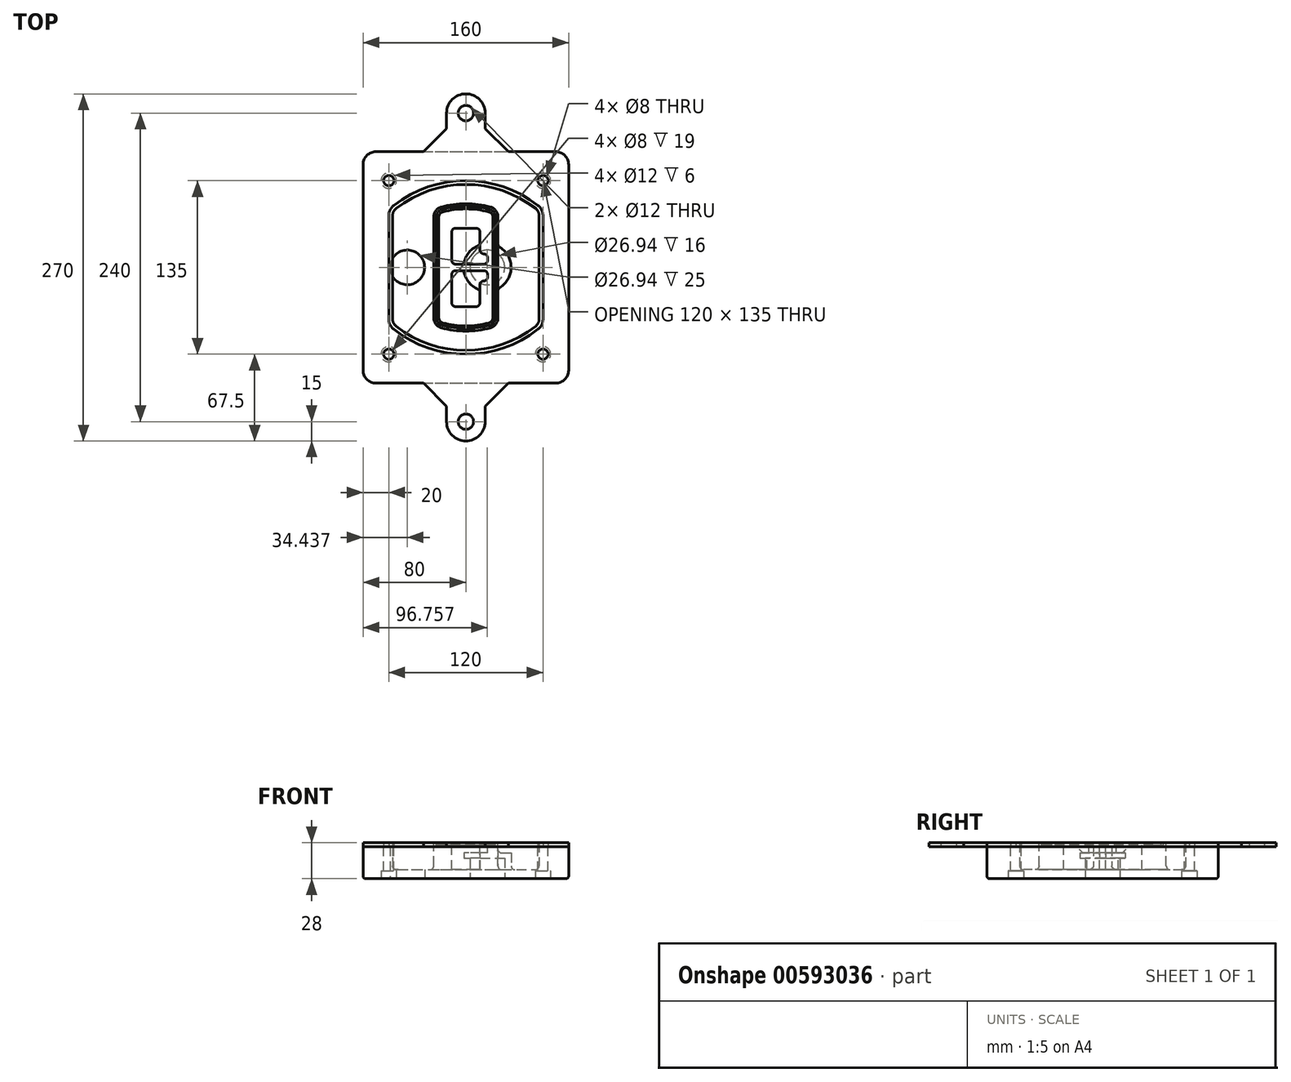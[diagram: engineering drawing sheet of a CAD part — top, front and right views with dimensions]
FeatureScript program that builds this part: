
annotation { "Feature Type Name" : "Feature", "Feature Type Description" : "" }
export const myFeature = defineFeature(function(context is Context, id is Id, definition is map)
    precondition{}
    {
        {
            var Q0;
            Q0=qCreatedBy(makeId("Top.planeOp"),FACE);
            var sketch = newSketch(context, id + "F0", { "sketchPlane" : qUnion([Q0])});
            skPoint(sketch, "E0.rect.middle", {"position": v(0, 0) * mm});
            skLineSegment(sketch, "E1.bottom", {"start": v(-70, -90) * mm, "end": v(70, -90) * mm});
            skLineSegment(sketch, "E1.top", {"start": v(-70, 90) * mm, "end": v(70, 90) * mm});
            skLineSegment(sketch, "E1.left", {"start": v(-80, -80) * mm, "end": v(-80, 80) * mm});
            skLineSegment(sketch, "E1.right", {"start": v(80, -80) * mm, "end": v(80, 80) * mm});
            skLineSegment(sketch, "E2", {"start": v(-80, 90) * mm, "end": v(80, -90) * mm, "construction": true});
            skLineSegment(sketch, "E3", {"start": v(80, 90) * mm, "end": v(-80, -90) * mm, "construction": true});
            skCircle(sketch, "E4", {"center": v(-60, 67.5) * mm, "radius": 4 * mm});
            skCircle(sketch, "E5", {"center": v(60, 67.5) * mm, "radius": 4 * mm});
            skCircle(sketch, "E6", {"center": v(60, -67.5) * mm, "radius": 4 * mm});
            skCircle(sketch, "E7", {"center": v(-60, -67.5) * mm, "radius": 4 * mm});
            skLineSegment(sketch, "E8", {"start": v(-60, 67.5) * mm, "end": v(60, 67.5) * mm, "construction": true});
            skLineSegment(sketch, "E9", {"start": v(60, 67.5) * mm, "end": v(60, -67.5) * mm, "construction": true});
            skLineSegment(sketch, "E10", {"start": v(60, -67.5) * mm, "end": v(-60, -67.5) * mm, "construction": true});
            skLineSegment(sketch, "E11", {"start": v(-60, -67.5) * mm, "end": v(-60, 67.5) * mm, "construction": true});
            skLineSegment(sketch, "E12", {"start": v(-60, 40.3) * mm, "end": v(-60, -40.3) * mm});
            skLineSegment(sketch, "E13", {"start": v(60, 40.3) * mm, "end": v(60, -40.3) * mm});
            skArc(sketch, "E14", {"start": v(56.15, 48.18) * mm, "mid": v(0, 67.5) * mm, "end": v(-56.15, 48.18) * mm});
            skArc(sketch, "E15", {"start": v(-56.15, -48.18) * mm, "mid": v(0, -67.5) * mm, "end": v(56.15, -48.18) * mm});
            skLineSegment(sketch, "E16", {"start": v(-60, 0) * mm, "end": v(60, 0) * mm, "construction": true});
            skPoint(sketch, "E17.visualSharp", {"position": v(-60, -45) * mm});
            skArc(sketch, "E17.filletArc", {"start": v(-60, -40.3) * mm, "mid": v(-58.99, -44.68) * mm, "end": v(-56.15, -48.18) * mm});
            skPoint(sketch, "E18.visualSharp", {"position": v(-60, 45) * mm});
            skArc(sketch, "E18.filletArc", {"start": v(-56.15, 48.18) * mm, "mid": v(-58.99, 44.68) * mm, "end": v(-60, 40.3) * mm});
            skPoint(sketch, "E19.visualSharp", {"position": v(60, 45) * mm});
            skArc(sketch, "E19.filletArc", {"start": v(60, 40.3) * mm, "mid": v(58.99, 44.68) * mm, "end": v(56.15, 48.18) * mm});
            skPoint(sketch, "E20.visualSharp", {"position": v(60, -45) * mm});
            skArc(sketch, "E20.filletArc", {"start": v(56.15, -48.18) * mm, "mid": v(58.99, -44.68) * mm, "end": v(60, -40.3) * mm});
            skPoint(sketch, "E21.visualSharp", {"position": v(-80, 90) * mm});
            skArc(sketch, "E21.filletArc", {"start": v(-70, 90) * mm, "mid": v(-77.07, 87.07) * mm, "end": v(-80, 80) * mm});
            skPoint(sketch, "E22.visualSharp", {"position": v(80, 90) * mm});
            skArc(sketch, "E22.filletArc", {"start": v(80, 80) * mm, "mid": v(77.07, 87.07) * mm, "end": v(70, 90) * mm});
            skPoint(sketch, "E23.visualSharp", {"position": v(80, -90) * mm});
            skArc(sketch, "E23.filletArc", {"start": v(70, -90) * mm, "mid": v(77.07, -87.07) * mm, "end": v(80, -80) * mm});
            skPoint(sketch, "E24.visualSharp", {"position": v(-80, -90) * mm});
            skArc(sketch, "E24.filletArc", {"start": v(-80, -80) * mm, "mid": v(-77.07, -87.07) * mm, "end": v(-70, -90) * mm});
            skArc(sketch, "E25.0", {"start": v(57, 40.3) * mm, "mid": v(56.3, 43.36) * mm, "end": v(54.3, 45.81) * mm});
            skLineSegment(sketch, "E25.1", {"start": v(57, 40.3) * mm, "end": v(57, -40.3) * mm});
            skArc(sketch, "E25.2", {"start": v(54.3, -45.81) * mm, "mid": v(56.3, -43.36) * mm, "end": v(57, -40.3) * mm});
            skArc(sketch, "E25.3", {"start": v(-54.3, -45.81) * mm, "mid": v(0, -64.5) * mm, "end": v(54.3, -45.81) * mm});
            skArc(sketch, "E25.4", {"start": v(-57, -40.3) * mm, "mid": v(-56.3, -43.36) * mm, "end": v(-54.3, -45.81) * mm});
            skArc(sketch, "E25.5", {"start": v(54.3, 45.81) * mm, "mid": v(0, 64.5) * mm, "end": v(-54.3, 45.81) * mm});
            skLineSegment(sketch, "E25.6", {"start": v(-57, 40.3) * mm, "end": v(-57, -40.3) * mm});
            skArc(sketch, "E25.7", {"start": v(-54.3, 45.81) * mm, "mid": v(-56.3, 43.36) * mm, "end": v(-57, 40.3) * mm});
            skArc(sketch, "E26.0", {"start": v(-58.62, 51.33) * mm, "mid": v(-62.58, 46.43) * mm, "end": v(-64, 40.3) * mm});
            skArc(sketch, "E26.1", {"start": v(58.62, 51.33) * mm, "mid": v(0, 71.5) * mm, "end": v(-58.62, 51.33) * mm});
            skArc(sketch, "E26.2", {"start": v(64, 40.3) * mm, "mid": v(62.58, 46.43) * mm, "end": v(58.62, 51.33) * mm});
            skLineSegment(sketch, "E26.3", {"start": v(64, 40.3) * mm, "end": v(64, -40.3) * mm});
            skArc(sketch, "E26.4", {"start": v(58.62, -51.33) * mm, "mid": v(62.58, -46.43) * mm, "end": v(64, -40.3) * mm});
            skLineSegment(sketch, "E26.5", {"start": v(-64, 40.3) * mm, "end": v(-64, -40.3) * mm});
            skArc(sketch, "E26.6", {"start": v(-58.62, -51.33) * mm, "mid": v(0, -71.5) * mm, "end": v(58.62, -51.33) * mm});
            skArc(sketch, "E26.7", {"start": v(-64, -40.3) * mm, "mid": v(-62.58, -46.43) * mm, "end": v(-58.62, -51.33) * mm});
            skSolve(sketch);
        }
        {
            var Q0;
            Q0=makeQuery(id+"F0.imprint","IMPRINT",FACE,{"disambiguationData":[TD([[makeQuery(id+"F0.imprint","IMPRINT",EDGE,{"derivedFrom":sQuery(id+"F0.wireOp",EDGE,"E1.bottom")}),1.0]])]});
            var Q1;
            Q1=makeQuery(id+"F0.imprint","IMPRINT",FACE,{"disambiguationData":[TD([[makeQuery(id+"F0.imprint","IMPRINT",EDGE,{"derivedFrom":sQuery(id+"F0.wireOp",EDGE,"E12")}),1.0]])]});
            var Q2;
            Q2=makeQuery(id+"F0.imprint","IMPRINT",FACE,{"disambiguationData":[TD([[makeQuery(id+"F0.imprint","IMPRINT",EDGE,{"derivedFrom":sQuery(id+"F0.wireOp",EDGE,"E25.0")}),1.0]])]});
            var Q3;
            Q3=makeQuery(id+"F0.imprint","IMPRINT",FACE,{"disambiguationData":[TD([[makeQuery(id+"F0.imprint","IMPRINT",EDGE,{"derivedFrom":sQuery(id+"F0.wireOp",EDGE,"E12")}),-1.0]])]});
            extrude(context, id + "F1", {"entities" : qUnion([Q0, Q1, Q2, Q3]), "oppositeDirection" : true, "depth" : 25 * mm});
        }
        {
            var Q0;
            Q0=makeQuery(id+"F0.imprint","IMPRINT",FACE,{"disambiguationData":[TD([[makeQuery(id+"F0.imprint","IMPRINT",EDGE,{"derivedFrom":sQuery(id+"F0.wireOp",EDGE,"E12")}),1.0]])]});
            extrude(context, id + "F2", {"entities" : qUnion([Q0]), "operationType" : NewBodyOperationType.ADD, "depth" : 3 * mm});
        }
        {
            var Q0;
            Q0=makeQuery(id+"F0.imprint","IMPRINT",FACE,{"disambiguationData":[TD([[makeQuery(id+"F0.imprint","IMPRINT",EDGE,{"derivedFrom":sQuery(id+"F0.wireOp",EDGE,"E25.0")}),1.0]])]});
            extrude(context, id + "F3", {"entities" : qUnion([Q0]), "operationType" : NewBodyOperationType.REMOVE, "oppositeDirection" : true, "depth" : 18 * mm});
        }
        {
            var Q0;
            Q0=makeQuery(id+"F2.opExtrude","CAP_FACE",FACE,{"disambiguationData":[OSD([sQuery(id+"F0.wireOp",EDGE,"E12"),sQuery(id+"F0.wireOp",EDGE,"E13"),sQuery(id+"F0.wireOp",EDGE,"E14"),sQuery(id+"F0.wireOp",EDGE,"E15"),sQuery(id+"F0.wireOp",EDGE,"E17.filletArc"),sQuery(id+"F0.wireOp",EDGE,"E18.filletArc"),sQuery(id+"F0.wireOp",EDGE,"E19.filletArc"),sQuery(id+"F0.wireOp",EDGE,"E20.filletArc"),sQuery(id+"F0.wireOp",EDGE,"E25.0"),sQuery(id+"F0.wireOp",EDGE,"E25.1"),sQuery(id+"F0.wireOp",EDGE,"E25.2"),sQuery(id+"F0.wireOp",EDGE,"E25.3"),sQuery(id+"F0.wireOp",EDGE,"E25.4"),sQuery(id+"F0.wireOp",EDGE,"E25.5"),sQuery(id+"F0.wireOp",EDGE,"E25.6"),sQuery(id+"F0.wireOp",EDGE,"E25.7")])],"isStart":false});
            var sketch = newSketch(context, id + "F4", { "sketchPlane" : qUnion([Q0])});
            skArc(sketch, "E27.0", {"start": v(-19.08, -46.97) * mm, "mid": v(0, -49.5) * mm, "end": v(19.08, -46.97) * mm});
            skArc(sketch, "E28.0", {"start": v(19.08, 46.97) * mm, "mid": v(0, 49.5) * mm, "end": v(-19.08, 46.97) * mm});
            skLineSegment(sketch, "E29", {"start": v(-25, 39.25) * mm, "end": v(-25, -39.25) * mm});
            skLineSegment(sketch, "E30", {"start": v(25, 39.25) * mm, "end": v(25, -39.25) * mm});
            skLineSegment(sketch, "E31", {"start": v(-25, 45.1) * mm, "end": v(25, 45.1) * mm, "construction": true});
            skLineSegment(sketch, "E32", {"start": v(-25, -45.1) * mm, "end": v(25, -45.1) * mm, "construction": true});
            skPoint(sketch, "E33.visualSharp", {"position": v(-25, 45.1) * mm});
            skArc(sketch, "E33.filletArc", {"start": v(-19.08, 46.97) * mm, "mid": v(-23.35, 44.11) * mm, "end": v(-25, 39.25) * mm});
            skPoint(sketch, "E34.visualSharp", {"position": v(25, 45.1) * mm});
            skArc(sketch, "E34.filletArc", {"start": v(25, 39.25) * mm, "mid": v(23.35, 44.11) * mm, "end": v(19.08, 46.97) * mm});
            skPoint(sketch, "E35.visualSharp", {"position": v(25, -45.1) * mm});
            skArc(sketch, "E35.filletArc", {"start": v(19.08, -46.97) * mm, "mid": v(23.35, -44.11) * mm, "end": v(25, -39.25) * mm});
            skPoint(sketch, "E36.visualSharp", {"position": v(-25, -45.1) * mm});
            skArc(sketch, "E36.filletArc", {"start": v(-25, -39.25) * mm, "mid": v(-23.35, -44.11) * mm, "end": v(-19.08, -46.97) * mm});
            skArc(sketch, "E37.0", {"start": v(54.3, 45.81) * mm, "mid": v(0, 64.5) * mm, "end": v(-54.3, 45.81) * mm});
            skArc(sketch, "E37.1", {"start": v(-54.3, 45.81) * mm, "mid": v(-56.3, 43.36) * mm, "end": v(-57, 40.3) * mm});
            skLineSegment(sketch, "E37.2", {"start": v(-57, 40.3) * mm, "end": v(-57, -40.3) * mm});
            skArc(sketch, "E37.3", {"start": v(-57, -40.3) * mm, "mid": v(-56.3, -43.36) * mm, "end": v(-54.3, -45.81) * mm});
            skArc(sketch, "E37.4", {"start": v(-54.3, -45.81) * mm, "mid": v(0, -64.5) * mm, "end": v(54.3, -45.81) * mm});
            skArc(sketch, "E37.5", {"start": v(54.3, -45.81) * mm, "mid": v(56.3, -43.36) * mm, "end": v(57, -40.3) * mm});
            skLineSegment(sketch, "E37.6", {"start": v(57, 40.3) * mm, "end": v(57, -40.3) * mm});
            skArc(sketch, "E37.7", {"start": v(57, 40.3) * mm, "mid": v(56.3, 43.36) * mm, "end": v(54.3, 45.81) * mm});
            skLineSegment(sketch, "E38.0", {"start": v(23, 39.25) * mm, "end": v(23, -39.25) * mm});
            skArc(sketch, "E38.1", {"start": v(18.56, -45.04) * mm, "mid": v(21.76, -42.9) * mm, "end": v(23, -39.25) * mm});
            skArc(sketch, "E38.2", {"start": v(-18.56, -45.04) * mm, "mid": v(0, -47.5) * mm, "end": v(18.56, -45.04) * mm});
            skArc(sketch, "E38.3", {"start": v(-23, -39.25) * mm, "mid": v(-21.76, -42.9) * mm, "end": v(-18.56, -45.04) * mm});
            skLineSegment(sketch, "E38.4", {"start": v(-23, 39.25) * mm, "end": v(-23, -39.25) * mm});
            skArc(sketch, "E38.5", {"start": v(23, 39.25) * mm, "mid": v(21.76, 42.9) * mm, "end": v(18.56, 45.04) * mm});
            skArc(sketch, "E38.6", {"start": v(-18.56, 45.04) * mm, "mid": v(-21.76, 42.9) * mm, "end": v(-23, 39.25) * mm});
            skArc(sketch, "E38.7", {"start": v(18.56, 45.04) * mm, "mid": v(0, 47.5) * mm, "end": v(-18.56, 45.04) * mm});
            skArc(sketch, "E39.0", {"start": v(21, 39.25) * mm, "mid": v(20.18, 41.68) * mm, "end": v(18.04, 43.1) * mm});
            skLineSegment(sketch, "E39.1", {"start": v(21, 39.25) * mm, "end": v(21, -39.25) * mm});
            skArc(sketch, "E39.2", {"start": v(18.04, -43.1) * mm, "mid": v(20.18, -41.68) * mm, "end": v(21, -39.25) * mm});
            skArc(sketch, "E39.3", {"start": v(-18.04, -43.1) * mm, "mid": v(0, -45.5) * mm, "end": v(18.04, -43.1) * mm});
            skArc(sketch, "E39.4", {"start": v(-21, -39.25) * mm, "mid": v(-20.18, -41.68) * mm, "end": v(-18.04, -43.1) * mm});
            skArc(sketch, "E39.5", {"start": v(18.04, 43.1) * mm, "mid": v(0, 45.5) * mm, "end": v(-18.04, 43.1) * mm});
            skLineSegment(sketch, "E39.6", {"start": v(-21, 39.25) * mm, "end": v(-21, -39.25) * mm});
            skArc(sketch, "E39.7", {"start": v(-18.04, 43.1) * mm, "mid": v(-20.18, 41.68) * mm, "end": v(-21, 39.25) * mm});
            skLineSegment(sketch, "E40", {"start": v(-25, 0) * mm, "end": v(25, 0) * mm, "construction": true});
            skLineSegment(sketch, "E41", {"start": v(-11, 5.5) * mm, "end": v(-11, 27.5) * mm});
            skLineSegment(sketch, "E42", {"start": v(-8, 30.5) * mm, "end": v(8, 30.5) * mm});
            skLineSegment(sketch, "E43", {"start": v(11, 27.5) * mm, "end": v(11, 13.5) * mm});
            skLineSegment(sketch, "E44", {"start": v(14, 10.5) * mm, "end": v(14, 10.5) * mm});
            skLineSegment(sketch, "E45", {"start": v(17, 7.5) * mm, "end": v(17, 5.5) * mm});
            skLineSegment(sketch, "E46", {"start": v(14, 2.5) * mm, "end": v(-8, 2.5) * mm});
            skPoint(sketch, "E47.visualSharp", {"position": v(-11, 30.5) * mm});
            skArc(sketch, "E47.filletArc", {"start": v(-8, 30.5) * mm, "mid": v(-10.12, 29.62) * mm, "end": v(-11, 27.5) * mm});
            skPoint(sketch, "E48.visualSharp", {"position": v(11, 30.5) * mm});
            skArc(sketch, "E48.filletArc", {"start": v(11, 27.5) * mm, "mid": v(10.12, 29.62) * mm, "end": v(8, 30.5) * mm});
            skPoint(sketch, "E49.visualSharp", {"position": v(11, 10.5) * mm});
            skArc(sketch, "E49.filletArc", {"start": v(11, 13.5) * mm, "mid": v(11.88, 11.38) * mm, "end": v(14, 10.5) * mm});
            skPoint(sketch, "E50.visualSharp", {"position": v(17, 10.5) * mm});
            skArc(sketch, "E50.filletArc", {"start": v(17, 7.5) * mm, "mid": v(16.12, 9.62) * mm, "end": v(14, 10.5) * mm});
            skPoint(sketch, "E51.visualSharp", {"position": v(17, 2.5) * mm});
            skArc(sketch, "E51.filletArc", {"start": v(14, 2.5) * mm, "mid": v(16.12, 3.38) * mm, "end": v(17, 5.5) * mm});
            skPoint(sketch, "E52.visualSharp", {"position": v(-11, 2.5) * mm});
            skArc(sketch, "E52.filletArc", {"start": v(-11, 5.5) * mm, "mid": v(-10.12, 3.38) * mm, "end": v(-8, 2.5) * mm});
            skLineSegment(sketch, "E53.0.MirrorCS", {"start": v(14, -2.5) * mm, "end": v(-8, -2.5) * mm});
            skArc(sketch, "E54.0.MirrorCS", {"start": v(-11, -5.5) * mm, "mid": v(-10.12, -3.38) * mm, "end": v(-8, -2.5) * mm});
            skLineSegment(sketch, "E55.0.MirrorCS", {"start": v(-11, -5.5) * mm, "end": v(-11, -27.5) * mm});
            skArc(sketch, "E56.0.MirrorCS", {"start": v(-8, -30.5) * mm, "mid": v(-10.12, -29.62) * mm, "end": v(-11, -27.5) * mm});
            skLineSegment(sketch, "E57.0.MirrorCS", {"start": v(-8, -30.5) * mm, "end": v(8, -30.5) * mm});
            skArc(sketch, "E58.0.MirrorCS", {"start": v(11, -27.5) * mm, "mid": v(10.12, -29.62) * mm, "end": v(8, -30.5) * mm});
            skLineSegment(sketch, "E59.0.MirrorCS", {"start": v(11, -27.5) * mm, "end": v(11, -13.5) * mm});
            skArc(sketch, "E60.0.MirrorCS", {"start": v(11, -13.5) * mm, "mid": v(11.88, -11.38) * mm, "end": v(14, -10.5) * mm});
            skArc(sketch, "E61.0.MirrorCS", {"start": v(17, -7.5) * mm, "mid": v(16.12, -9.62) * mm, "end": v(14, -10.5) * mm});
            skLineSegment(sketch, "E62.0.MirrorCS", {"start": v(17, -7.5) * mm, "end": v(17, -5.5) * mm});
            skArc(sketch, "E63.0.MirrorCS", {"start": v(14, -2.5) * mm, "mid": v(16.12, -3.38) * mm, "end": v(17, -5.5) * mm});
            skSolve(sketch);
        }
        {
            var Q0;
            Q0=makeQuery(id+"F4.imprint","IMPRINT",FACE,{"disambiguationData":[TD([[makeQuery(id+"F4.imprint","IMPRINT",EDGE,{"derivedFrom":sQuery(id+"F4.wireOp",EDGE,"E27.0")}),1.0]])]});
            var Q1;
            Q1=makeQuery(id+"F4.imprint","IMPRINT",FACE,{"disambiguationData":[TD([[makeQuery(id+"F4.imprint","IMPRINT",EDGE,{"derivedFrom":sQuery(id+"F4.wireOp",EDGE,"E38.0")}),-1.0]])]});
            var Q2;
            Q2=makeQuery(id+"F4.imprint","IMPRINT",FACE,{"disambiguationData":[TD([[makeQuery(id+"F4.imprint","IMPRINT",EDGE,{"derivedFrom":sQuery(id+"F4.wireOp",EDGE,"E39.0")}),1.0]])]});
            extrude(context, id + "F5", {"entities" : qUnion([Q0, Q1, Q2]), "operationType" : NewBodyOperationType.ADD, "endBound" : BoundingType.UP_TO_NEXT, "oppositeDirection" : true, "depth" : 25 * mm});
        }
        {
            var Q0;
            Q0=makeQuery(id+"F4.imprint","IMPRINT",FACE,{"disambiguationData":[TD([[makeQuery(id+"F4.imprint","IMPRINT",EDGE,{"derivedFrom":sQuery(id+"F4.wireOp",EDGE,"E38.0")}),-1.0]])]});
            extrude(context, id + "F6", {"entities" : qUnion([Q0]), "operationType" : NewBodyOperationType.REMOVE, "oppositeDirection" : true, "depth" : 2 * mm});
        }
        {
            var Q0;
            Q0=makeQuery(id+"F1.opExtrude","CAP_FACE",FACE,{"disambiguationData":[OSD([sQuery(id+"F0.wireOp",EDGE,"E1.bottom"),sQuery(id+"F0.wireOp",EDGE,"E1.top"),sQuery(id+"F0.wireOp",EDGE,"E1.left"),sQuery(id+"F0.wireOp",EDGE,"E1.right"),sQuery(id+"F0.wireOp",EDGE,"E4"),sQuery(id+"F0.wireOp",EDGE,"E5"),sQuery(id+"F0.wireOp",EDGE,"E6"),sQuery(id+"F0.wireOp",EDGE,"E7"),sQuery(id+"F0.wireOp",EDGE,"E21.filletArc"),sQuery(id+"F0.wireOp",EDGE,"E22.filletArc"),sQuery(id+"F0.wireOp",EDGE,"E23.filletArc"),sQuery(id+"F0.wireOp",EDGE,"E24.filletArc")])],"isStart":false});
            var sketch = newSketch(context, id + "F7", { "sketchPlane" : qUnion([Q0])});
            skCircle(sketch, "E64", {"center": v(16.76, 0) * mm, "radius": 13.47 * mm});
            skCircle(sketch, "E65", {"center": v(-45.56, 0) * mm, "radius": 13.47 * mm});
            skLineSegment(sketch, "E66", {"start": v(80, 0) * mm, "end": v(-80, 0) * mm});
            skCircle(sketch, "E67", {"center": v(16.76, 0) * mm, "radius": 18.47 * mm});
            skCircle(sketch, "E68", {"center": v(60, -67.5) * mm, "radius": 6 * mm});
            skCircle(sketch, "E69", {"center": v(-60, -67.5) * mm, "radius": 6 * mm});
            skCircle(sketch, "E70", {"center": v(-60, 67.5) * mm, "radius": 6 * mm});
            skCircle(sketch, "E71", {"center": v(60, 67.5) * mm, "radius": 6 * mm});
            skSolve(sketch);
        }
        {
            var Q0;
            {var subQ1=sQuery(id+"F7.wireOp",EDGE,"E66");var subQ4=sQuery(id+"F7.wireOp",EDGE,"E64");var subQ6=makeQuery(id+"F7.imprint","INTERSECT",VERTEX,{"disambiguationData":[OD(0.0)],"derivedFrom":[subQ4,subQ1]});Q0=makeQuery(id+"F7.imprint","IMPRINT",FACE,{"disambiguationData":[TD([[makeQuery(id+"F7.imprint","IMPRINT",EDGE,{"disambiguationData":[TD([[subQ6,-1.0]])],"derivedFrom":subQ4}),-1.0]])]});}
            var Q1;
            {var subQ0=sQuery(id+"F7.wireOp",EDGE,"E66");var subQ1=sQuery(id+"F7.wireOp",EDGE,"E64");var subQ3=makeQuery(id+"F7.imprint","INTERSECT",VERTEX,{"disambiguationData":[OD(0.0)],"derivedFrom":[subQ1,subQ0]});Q1=makeQuery(id+"F7.imprint","IMPRINT",FACE,{"disambiguationData":[TD([[makeQuery(id+"F7.imprint","IMPRINT",EDGE,{"disambiguationData":[TD([[subQ3,-1.0]])],"derivedFrom":subQ1}),1.0]])]});}
            var Q2;
            {var subQ0=sQuery(id+"F7.wireOp",EDGE,"E66");var subQ1=sQuery(id+"F7.wireOp",EDGE,"E64");var subQ3=makeQuery(id+"F7.imprint","INTERSECT",VERTEX,{"disambiguationData":[OD(0.0)],"derivedFrom":[subQ1,subQ0]});Q2=makeQuery(id+"F7.imprint","IMPRINT",FACE,{"disambiguationData":[TD([[makeQuery(id+"F7.imprint","IMPRINT",EDGE,{"disambiguationData":[TD([[subQ3,1.0]])],"derivedFrom":subQ1}),1.0]])]});}
            var Q3;
            {var subQ1=sQuery(id+"F7.wireOp",EDGE,"E66");var subQ4=sQuery(id+"F7.wireOp",EDGE,"E64");var subQ6=makeQuery(id+"F7.imprint","INTERSECT",VERTEX,{"disambiguationData":[OD(0.0)],"derivedFrom":[subQ4,subQ1]});Q3=makeQuery(id+"F7.imprint","IMPRINT",FACE,{"disambiguationData":[TD([[makeQuery(id+"F7.imprint","IMPRINT",EDGE,{"disambiguationData":[TD([[subQ6,1.0]])],"derivedFrom":subQ4}),-1.0]])]});}
            extrude(context, id + "F8", {"entities" : qUnion([Q0, Q1, Q2, Q3]), "operationType" : NewBodyOperationType.ADD, "oppositeDirection" : true, "depth" : 20 * mm});
        }
        {
            var Q0;
            {var subQ0=sQuery(id+"F7.wireOp",EDGE,"E66");var subQ1=sQuery(id+"F7.wireOp",EDGE,"E64");var subQ3=makeQuery(id+"F7.imprint","INTERSECT",VERTEX,{"disambiguationData":[OD(0.0)],"derivedFrom":[subQ1,subQ0]});Q0=makeQuery(id+"F7.imprint","IMPRINT",FACE,{"disambiguationData":[TD([[makeQuery(id+"F7.imprint","IMPRINT",EDGE,{"disambiguationData":[TD([[subQ3,-1.0]])],"derivedFrom":subQ1}),1.0]])]});}
            var Q1;
            {var subQ0=sQuery(id+"F7.wireOp",EDGE,"E66");var subQ1=sQuery(id+"F7.wireOp",EDGE,"E64");var subQ3=makeQuery(id+"F7.imprint","INTERSECT",VERTEX,{"disambiguationData":[OD(0.0)],"derivedFrom":[subQ1,subQ0]});Q1=makeQuery(id+"F7.imprint","IMPRINT",FACE,{"disambiguationData":[TD([[makeQuery(id+"F7.imprint","IMPRINT",EDGE,{"disambiguationData":[TD([[subQ3,1.0]])],"derivedFrom":subQ1}),1.0]])]});}
            extrude(context, id + "F9", {"entities" : qUnion([Q0, Q1]), "operationType" : NewBodyOperationType.REMOVE, "oppositeDirection" : true, "depth" : 16 * mm});
        }
        {
            var Q0;
            {var subQ0=sQuery(id+"F7.wireOp",EDGE,"E66");var subQ1=sQuery(id+"F7.wireOp",EDGE,"E65");var subQ3=makeQuery(id+"F7.imprint","INTERSECT",VERTEX,{"disambiguationData":[OD(0.0)],"derivedFrom":[subQ1,subQ0]});Q0=makeQuery(id+"F7.imprint","IMPRINT",FACE,{"disambiguationData":[TD([[makeQuery(id+"F7.imprint","IMPRINT",EDGE,{"disambiguationData":[TD([[subQ3,-1.0]])],"derivedFrom":subQ1}),1.0]])]});}
            var Q1;
            {var subQ0=sQuery(id+"F7.wireOp",EDGE,"E66");var subQ1=sQuery(id+"F7.wireOp",EDGE,"E65");var subQ3=makeQuery(id+"F7.imprint","INTERSECT",VERTEX,{"disambiguationData":[OD(0.0)],"derivedFrom":[subQ1,subQ0]});Q1=makeQuery(id+"F7.imprint","IMPRINT",FACE,{"disambiguationData":[TD([[makeQuery(id+"F7.imprint","IMPRINT",EDGE,{"disambiguationData":[TD([[subQ3,1.0]])],"derivedFrom":subQ1}),1.0]])]});}
            extrude(context, id + "F10", {"entities" : qUnion([Q0, Q1]), "operationType" : NewBodyOperationType.REMOVE, "oppositeDirection" : true, "depth" : 25 * mm});
        }
        {
            var Q0;
            Q0=makeQuery(id+"F7.imprint","IMPRINT",FACE,{"disambiguationData":[TD([[makeQuery(id+"F7.imprint","IMPRINT",EDGE,{"derivedFrom":sQuery(id+"F7.wireOp",EDGE,"E68")}),1.0]])]});
            var Q1;
            Q1=makeQuery(id+"F7.imprint","IMPRINT",FACE,{"disambiguationData":[TD([[makeQuery(id+"F7.imprint","IMPRINT",EDGE,{"derivedFrom":makeQuery(id+"F1.opExtrude","CAP_EDGE",EDGE,{"disambiguationData":[OSD([sQuery(id+"F0.wireOp",EDGE,"E5")])],"isStart":false})}),-1.0]])]});
            var Q2;
            Q2=makeQuery(id+"F7.imprint","IMPRINT",FACE,{"disambiguationData":[TD([[makeQuery(id+"F7.imprint","IMPRINT",EDGE,{"derivedFrom":sQuery(id+"F7.wireOp",EDGE,"E69")}),1.0]])]});
            var Q3;
            Q3=makeQuery(id+"F7.imprint","IMPRINT",FACE,{"disambiguationData":[TD([[makeQuery(id+"F7.imprint","IMPRINT",EDGE,{"derivedFrom":makeQuery(id+"F1.opExtrude","CAP_EDGE",EDGE,{"disambiguationData":[OSD([sQuery(id+"F0.wireOp",EDGE,"E4")])],"isStart":false})}),-1.0]])]});
            var Q4;
            Q4=makeQuery(id+"F7.imprint","IMPRINT",FACE,{"disambiguationData":[TD([[makeQuery(id+"F7.imprint","IMPRINT",EDGE,{"derivedFrom":sQuery(id+"F7.wireOp",EDGE,"E70")}),1.0]])]});
            var Q5;
            Q5=makeQuery(id+"F7.imprint","IMPRINT",FACE,{"disambiguationData":[TD([[makeQuery(id+"F7.imprint","IMPRINT",EDGE,{"derivedFrom":makeQuery(id+"F1.opExtrude","CAP_EDGE",EDGE,{"disambiguationData":[OSD([sQuery(id+"F0.wireOp",EDGE,"E7")])],"isStart":false})}),-1.0]])]});
            var Q6;
            Q6=makeQuery(id+"F7.imprint","IMPRINT",FACE,{"disambiguationData":[TD([[makeQuery(id+"F7.imprint","IMPRINT",EDGE,{"derivedFrom":sQuery(id+"F7.wireOp",EDGE,"E71")}),1.0]])]});
            var Q7;
            Q7=makeQuery(id+"F7.imprint","IMPRINT",FACE,{"disambiguationData":[TD([[makeQuery(id+"F7.imprint","IMPRINT",EDGE,{"derivedFrom":makeQuery(id+"F1.opExtrude","CAP_EDGE",EDGE,{"disambiguationData":[OSD([sQuery(id+"F0.wireOp",EDGE,"E6")])],"isStart":false})}),-1.0]])]});
            extrude(context, id + "F11", {"entities" : qUnion([Q0, Q1, Q2, Q3, Q4, Q5, Q6, Q7]), "operationType" : NewBodyOperationType.REMOVE, "oppositeDirection" : true, "depth" : 6 * mm});
        }
        {
            var Q0;
            Q0=makeQuery(id+"F9.boolean.opBoolean","COPY",FACE,{"derivedFrom":makeQuery(id+"F9.opExtrude","CAP_FACE",FACE,{"disambiguationData":[OSD([sQuery(id+"F7.wireOp",EDGE,"E64")])],"isStart":false})});
            var sketch = newSketch(context, id + "F12", { "sketchPlane" : qUnion([Q0])});
            skArc(sketch, "E72.0", {"start": v(11, 17.55) * mm, "mid": v(2.57, 11.82) * mm, "end": v(-1.54, 2.5) * mm});
            skArc(sketch, "E72.1", {"start": v(-1.54, -2.5) * mm, "mid": v(2.57, -11.82) * mm, "end": v(11, -17.55) * mm});
            skLineSegment(sketch, "E73", {"start": v(-1.54, -2.5) * mm, "end": v(14, -2.5) * mm});
            skLineSegment(sketch, "E74.0", {"start": v(14, 2.5) * mm, "end": v(-1.54, 2.5) * mm});
            skArc(sketch, "E74.1", {"start": v(14, 2.5) * mm, "mid": v(16.12, 3.38) * mm, "end": v(17, 5.5) * mm});
            skLineSegment(sketch, "E74.2", {"start": v(17, 7.5) * mm, "end": v(17, 5.5) * mm});
            skArc(sketch, "E74.3", {"start": v(17, 7.5) * mm, "mid": v(16.12, 9.62) * mm, "end": v(14, 10.5) * mm});
            skArc(sketch, "E74.4", {"start": v(11, 13.5) * mm, "mid": v(11.88, 11.38) * mm, "end": v(14, 10.5) * mm});
            skLineSegment(sketch, "E74.5", {"start": v(11, 17.55) * mm, "end": v(11, 13.5) * mm});
            skLineSegment(sketch, "E74.7", {"start": v(14, -2.5) * mm, "end": v(-1.54, -2.5) * mm});
            skArc(sketch, "E74.8", {"start": v(14, -2.5) * mm, "mid": v(16.12, -3.38) * mm, "end": v(17, -5.5) * mm});
            skLineSegment(sketch, "E74.9", {"start": v(17, -7.5) * mm, "end": v(17, -5.5) * mm});
            skArc(sketch, "E74.10", {"start": v(17, -7.5) * mm, "mid": v(16.12, -9.62) * mm, "end": v(14, -10.5) * mm});
            skArc(sketch, "E74.11", {"start": v(11, -13.5) * mm, "mid": v(11.88, -11.38) * mm, "end": v(14, -10.5) * mm});
            skLineSegment(sketch, "E74.12", {"start": v(11, -17.55) * mm, "end": v(11, -13.5) * mm});
            skPoint(sketch, "E75.orphan", {"position": v(11, -27.5) * mm});
            skPoint(sketch, "E76.orphan", {"position": v(-8, -2.5) * mm});
            skPoint(sketch, "E77.orphan", {"position": v(-8, 2.5) * mm});
            skPoint(sketch, "E78.orphan", {"position": v(11, 27.5) * mm});
            skSolve(sketch);
        }
        {
            var Q0;
            {var subQ7=sQuery(id+"F12.wireOp",EDGE,"E72.0");var subQ14=sQuery(id+"F12.wireOp",EDGE,"E72.1");var subQ16=sQuery(id+"F12.wireOp",EDGE,"E74.1");var subQ18=sQuery(id+"F12.wireOp",EDGE,"E74.8");Q0=qUnion([makeQuery(id+"F12.imprint","IMPRINT",FACE,{"disambiguationData":[TD([[makeQuery(id+"F12.imprint","IMPRINT",EDGE,{"derivedFrom":subQ7}),1.0]])]}),makeQuery(id+"F12.imprint","IMPRINT",FACE,{"disambiguationData":[TD([[makeQuery(id+"F12.imprint","IMPRINT",EDGE,{"derivedFrom":subQ14}),1.0]])]}),makeQuery(id+"F12.imprint","IMPRINT",FACE,{"disambiguationData":[TD([[makeQuery(id+"F12.imprint","IMPRINT",EDGE,{"derivedFrom":subQ16}),1.0]])]}),makeQuery(id+"F12.imprint","IMPRINT",FACE,{"disambiguationData":[TD([[makeQuery(id+"F12.imprint","IMPRINT",EDGE,{"derivedFrom":subQ18}),-1.0]])]})]);}
            var Q1;
            Q1=makeQuery(id+"F5.boolean.opBoolean","SPLIT",FACE,{"disambiguationData":[TD([makeQuery(id+"F5.opExtrude","SWEPT_FACE",FACE,{"disambiguationData":[OSD([sQuery(id+"F4.wireOp",EDGE,"E41")])]})])],"derivedFrom":makeQuery(id+"F3.boolean.opBoolean","COPY",FACE,{"derivedFrom":makeQuery(id+"F3.opExtrude","CAP_FACE",FACE,{"disambiguationData":[OSD([sQuery(id+"F0.wireOp",EDGE,"E25.0"),sQuery(id+"F0.wireOp",EDGE,"E25.1"),sQuery(id+"F0.wireOp",EDGE,"E25.2"),sQuery(id+"F0.wireOp",EDGE,"E25.3"),sQuery(id+"F0.wireOp",EDGE,"E25.4"),sQuery(id+"F0.wireOp",EDGE,"E25.5"),sQuery(id+"F0.wireOp",EDGE,"E25.6"),sQuery(id+"F0.wireOp",EDGE,"E25.7")])],"isStart":false})})});
            extrude(context, id + "F13", {"entities" : qUnion([Q0]), "operationType" : NewBodyOperationType.REMOVE, "endBound" : BoundingType.UP_TO_SURFACE, "endBoundEntityFace" : qUnion([Q1]), "depth" : 25 * mm});
        }
        {
            var Q0;
            Q0=makeQuery(id+"F3.boolean.opBoolean","COPY",EDGE,{"derivedFrom":makeQuery(id+"F3.opExtrude","CAP_EDGE",EDGE,{"disambiguationData":[OSD([sQuery(id+"F0.wireOp",EDGE,"E25.6")])],"isStart":false})});
            var Q1;
            Q1=makeQuery(id+"F8.boolean.opBoolean","INTERSECT",EDGE,{"derivedFrom":[makeQuery(id+"F5.opExtrude","SWEPT_FACE",FACE,{"disambiguationData":[OSD([sQuery(id+"F4.wireOp",EDGE,"E30")])]}),makeQuery(id+"F8.opExtrude","CAP_FACE",FACE,{"disambiguationData":[OSD([sQuery(id+"F7.wireOp",EDGE,"E67")])],"isStart":false})]});
            var Q2;
            Q2=makeQuery(id+"F8.boolean.opBoolean","INTERSECT",EDGE,{"disambiguationData":[OD(1.0)],"derivedFrom":[makeQuery(id+"F5.opExtrude","SWEPT_FACE",FACE,{"disambiguationData":[OSD([sQuery(id+"F4.wireOp",EDGE,"E30")])]}),makeQuery(id+"F8.opExtrude","SWEPT_FACE",FACE,{"disambiguationData":[OSD([sQuery(id+"F7.wireOp",EDGE,"E67")])]})]});
            var Q3;
            {var subQ0=sQuery(id+"F4.wireOp",EDGE,"E30");Q3=makeQuery(id+"F8.boolean.opBoolean","SPLIT",EDGE,{"disambiguationData":[TD([makeQuery(id+"F5.opExtrude","SWEPT_FACE",FACE,{"disambiguationData":[OSD([sQuery(id+"F4.wireOp",EDGE,"E35.filletArc")])]})])],"derivedFrom":makeQuery(id+"F5.opExtrude","CAP_EDGE",EDGE,{"disambiguationData":[OSD([subQ0])],"isStart":false})});}
            var Q4;
            {var subQ0=sQuery(id+"F0.wireOp",EDGE,"E25.7");var subQ1=sQuery(id+"F0.wireOp",EDGE,"E25.1");var subQ2=sQuery(id+"F0.wireOp",EDGE,"E25.6");var subQ3=sQuery(id+"F0.wireOp",EDGE,"E25.5");var subQ4=sQuery(id+"F0.wireOp",EDGE,"E25.4");var subQ5=sQuery(id+"F0.wireOp",EDGE,"E25.0");var subQ6=sQuery(id+"F0.wireOp",EDGE,"E25.2");var subQ7=sQuery(id+"F0.wireOp",EDGE,"E25.3");Q4=makeQuery(id+"F8.boolean.opBoolean","INTERSECT",EDGE,{"derivedFrom":[makeQuery(id+"F5.boolean.opBoolean","SPLIT",FACE,{"disambiguationData":[TD([makeQuery(id+"F2.opExtrude","SWEPT_FACE",FACE,{"disambiguationData":[OSD([subQ5])]})])],"derivedFrom":makeQuery(id+"F3.boolean.opBoolean","COPY",FACE,{"derivedFrom":makeQuery(id+"F3.opExtrude","CAP_FACE",FACE,{"disambiguationData":[OSD([subQ5,subQ1,subQ6,subQ7,subQ4,subQ3,subQ2,subQ0])],"isStart":false})})}),makeQuery(id+"F8.opExtrude","SWEPT_FACE",FACE,{"disambiguationData":[OSD([sQuery(id+"F7.wireOp",EDGE,"E67")])]})]});}
            var Q5;
            Q5=makeQuery(id+"F8.boolean.opBoolean","INTERSECT",EDGE,{"disambiguationData":[OD(0.0)],"derivedFrom":[makeQuery(id+"F5.opExtrude","SWEPT_FACE",FACE,{"disambiguationData":[OSD([sQuery(id+"F4.wireOp",EDGE,"E30")])]}),makeQuery(id+"F8.opExtrude","SWEPT_FACE",FACE,{"disambiguationData":[OSD([sQuery(id+"F7.wireOp",EDGE,"E67")])]})]});
            fillet(context, id + "F14", {"entities" : qUnion([Q0, Q1, Q2, Q3, Q4, Q5]), "radius" : 3 * mm, "tangentPropagation" : true, "allowEdgeOverflow" : false});
        }
        {
            var Q0;
            Q0=makeQuery(id+"F1.opExtrude","CAP_EDGE",EDGE,{"disambiguationData":[OSD([sQuery(id+"F0.wireOp",EDGE,"E1.bottom")])],"isStart":false});
            fillet(context, id + "F15", {"entities" : qUnion([Q0]), "radius" : 2 * mm, "tangentPropagation" : true, "allowEdgeOverflow" : false});
        }
        {
            var Q0;
            {var subQ0=sQuery(id+"F0.wireOp",EDGE,"E21.filletArc");var subQ1=sQuery(id+"F0.wireOp",EDGE,"E7");var subQ2=sQuery(id+"F0.wireOp",EDGE,"E6");var subQ3=sQuery(id+"F0.wireOp",EDGE,"E5");var subQ4=sQuery(id+"F0.wireOp",EDGE,"E4");var subQ5=sQuery(id+"F0.wireOp",EDGE,"E22.filletArc");var subQ6=sQuery(id+"F0.wireOp",EDGE,"E1.bottom");var subQ7=sQuery(id+"F0.wireOp",EDGE,"E1.right");var subQ8=sQuery(id+"F0.wireOp",EDGE,"E1.top");var subQ9=sQuery(id+"F0.wireOp",EDGE,"E1.left");var subQ10=sQuery(id+"F0.wireOp",EDGE,"E23.filletArc");var subQ11=sQuery(id+"F0.wireOp",EDGE,"E24.filletArc");Q0=makeQuery(id+"F2.boolean.opBoolean","SPLIT",FACE,{"disambiguationData":[TD([makeQuery(id+"F1.opExtrude","SWEPT_FACE",FACE,{"disambiguationData":[OSD([subQ6])]})])],"derivedFrom":makeQuery(id+"F1.opExtrude","CAP_FACE",FACE,{"disambiguationData":[OSD([subQ6,subQ8,subQ9,subQ7,subQ4,subQ3,subQ2,subQ1,subQ0,subQ5,subQ10,subQ11])],"isStart":true})});}
            var sketch = newSketch(context, id + "F16", { "sketchPlane" : qUnion([Q0])});
            skLineSegment(sketch, "E79", {"start": v(0, 90) * mm, "end": v(0, 120) * mm, "construction": true});
            skLineSegment(sketch, "E80", {"start": v(-15, 120) * mm, "end": v(-15, 108) * mm});
            skLineSegment(sketch, "E81", {"start": v(-15, 108) * mm, "end": v(-33, 90) * mm});
            skLineSegment(sketch, "E82.MirrorCS", {"start": v(15, 120) * mm, "end": v(15, 108) * mm});
            skLineSegment(sketch, "E83.MirrorCS", {"start": v(15, 108) * mm, "end": v(33, 90) * mm});
            skArc(sketch, "E84", {"start": v(-15, 120) * mm, "mid": v(0, 135) * mm, "end": v(15, 120) * mm});
            skLineSegment(sketch, "E85", {"start": v(0, 0) * mm, "end": v(-111.77, 0) * mm, "construction": true});
            skLineSegment(sketch, "E86.MirrorCS", {"start": v(-15, -120) * mm, "end": v(-15, -108) * mm});
            skLineSegment(sketch, "E87.MirrorCS", {"start": v(-15, -108) * mm, "end": v(-33, -90) * mm});
            skArc(sketch, "E88.MirrorCS", {"start": v(-15, -120) * mm, "mid": v(0, -135) * mm, "end": v(15, -120) * mm, "construction": true});
            skArc(sketch, "E89.MirrorCS", {"start": v(-15, -120) * mm, "mid": v(0, -135) * mm, "end": v(15, -120) * mm});
            skLineSegment(sketch, "E90.MirrorCS", {"start": v(15, -120) * mm, "end": v(15, -108) * mm});
            skLineSegment(sketch, "E91.MirrorCS", {"start": v(15, -108) * mm, "end": v(33, -90) * mm});
            skCircle(sketch, "E92", {"center": v(0, 120) * mm, "radius": 6 * mm});
            skCircle(sketch, "E93.MirrorC", {"center": v(0, -120) * mm, "radius": 6 * mm});
            skSolve(sketch);
        }
        {
            var Q0;
            Q0=makeQuery(id+"F16.imprint","IMPRINT",FACE,{"disambiguationData":[TD([[makeQuery(id+"F16.imprint","IMPRINT",EDGE,{"derivedFrom":makeQuery(id+"F1.opExtrude","CAP_EDGE",EDGE,{"disambiguationData":[OSD([sQuery(id+"F0.wireOp",EDGE,"E1.left")])],"isStart":true})}),-1.0]])]});
            var Q1;
            Q1=makeQuery(id+"F16.imprint","IMPRINT",FACE,{"disambiguationData":[TD([[makeQuery(id+"F16.imprint","IMPRINT",EDGE,{"derivedFrom":sQuery(id+"F16.wireOp",EDGE,"E80")}),1.0]])]});
            var Q2;
            Q2=makeQuery(id+"F16.imprint","IMPRINT",FACE,{"disambiguationData":[TD([[makeQuery(id+"F16.imprint","IMPRINT",EDGE,{"derivedFrom":sQuery(id+"F16.wireOp",EDGE,"E86.MirrorCS")}),-1.0]])]});
            var Q3;
            Q3=makeQuery(id+"F2.opExtrude","CAP_FACE",FACE,{"disambiguationData":[OSD([sQuery(id+"F0.wireOp",EDGE,"E12"),sQuery(id+"F0.wireOp",EDGE,"E13"),sQuery(id+"F0.wireOp",EDGE,"E14"),sQuery(id+"F0.wireOp",EDGE,"E15"),sQuery(id+"F0.wireOp",EDGE,"E17.filletArc"),sQuery(id+"F0.wireOp",EDGE,"E18.filletArc"),sQuery(id+"F0.wireOp",EDGE,"E19.filletArc"),sQuery(id+"F0.wireOp",EDGE,"E20.filletArc"),sQuery(id+"F0.wireOp",EDGE,"E25.0"),sQuery(id+"F0.wireOp",EDGE,"E25.1"),sQuery(id+"F0.wireOp",EDGE,"E25.2"),sQuery(id+"F0.wireOp",EDGE,"E25.3"),sQuery(id+"F0.wireOp",EDGE,"E25.4"),sQuery(id+"F0.wireOp",EDGE,"E25.5"),sQuery(id+"F0.wireOp",EDGE,"E25.6"),sQuery(id+"F0.wireOp",EDGE,"E25.7")])],"isStart":false});
            extrude(context, id + "F17", {"entities" : qUnion([Q0, Q1, Q2]), "endBound" : BoundingType.UP_TO_SURFACE, "depth" : 25 * mm, "endBoundEntityFace" : qUnion([Q3]), "offsetDistance" : 25 * mm});
        }
    });
